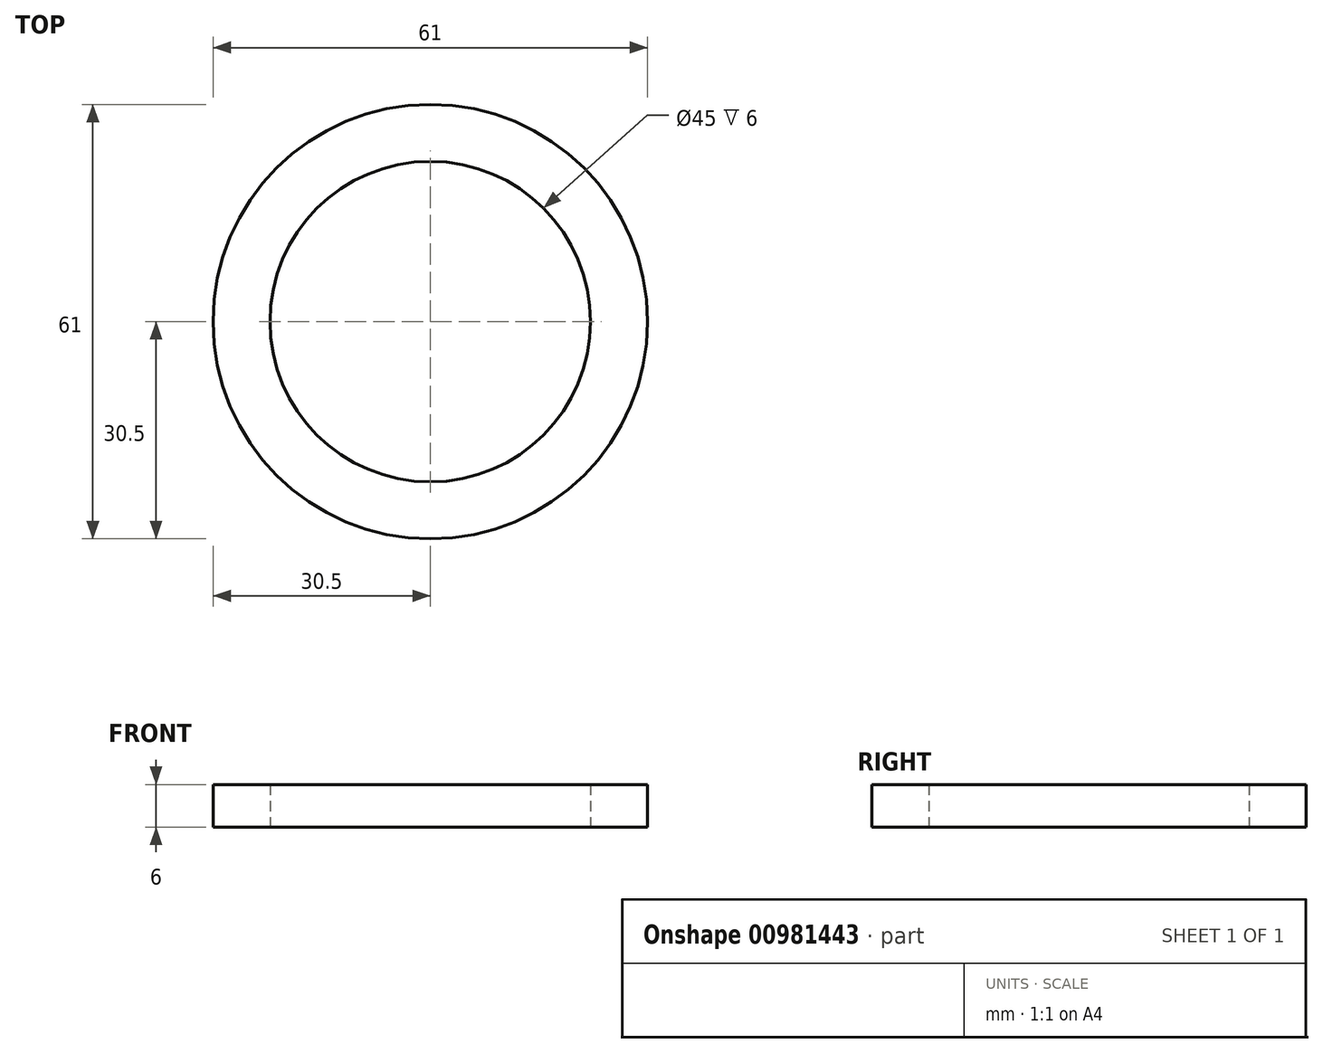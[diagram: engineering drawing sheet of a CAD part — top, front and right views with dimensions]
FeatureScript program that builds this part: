
annotation { "Feature Type Name" : "Feature", "Feature Type Description" : "" }
export const myFeature = defineFeature(function(context is Context, id is Id, definition is map)
    precondition{}
    {
        {
            var Q0;
            Q0=qCreatedBy(makeId("Top.planeOp"),FACE);
            var sketch = newSketch(context, id + "F0", { "sketchPlane" : qUnion([Q0])});
            skCircle(sketch, "E0", {"center": v(0, 0) * mm, "radius": 30.5 * mm});
            skCircle(sketch, "E1", {"center": v(0, 0) * mm, "radius": 22.5 * mm});
            skSolve(sketch);
        }
        {
            var Q0;
            Q0=makeQuery(id+"F0.imprint","IMPRINT",FACE,{"disambiguationData":[TD([[makeQuery(id+"F0.imprint","IMPRINT",EDGE,{"derivedFrom":sQuery(id+"F0.wireOp",EDGE,"E0")}),1.0]])]});
            extrude(context, id + "F1", {"entities" : qUnion([Q0]), "depth" : 6 * mm, "offsetDistance" : 25 * mm});
        }
    });
